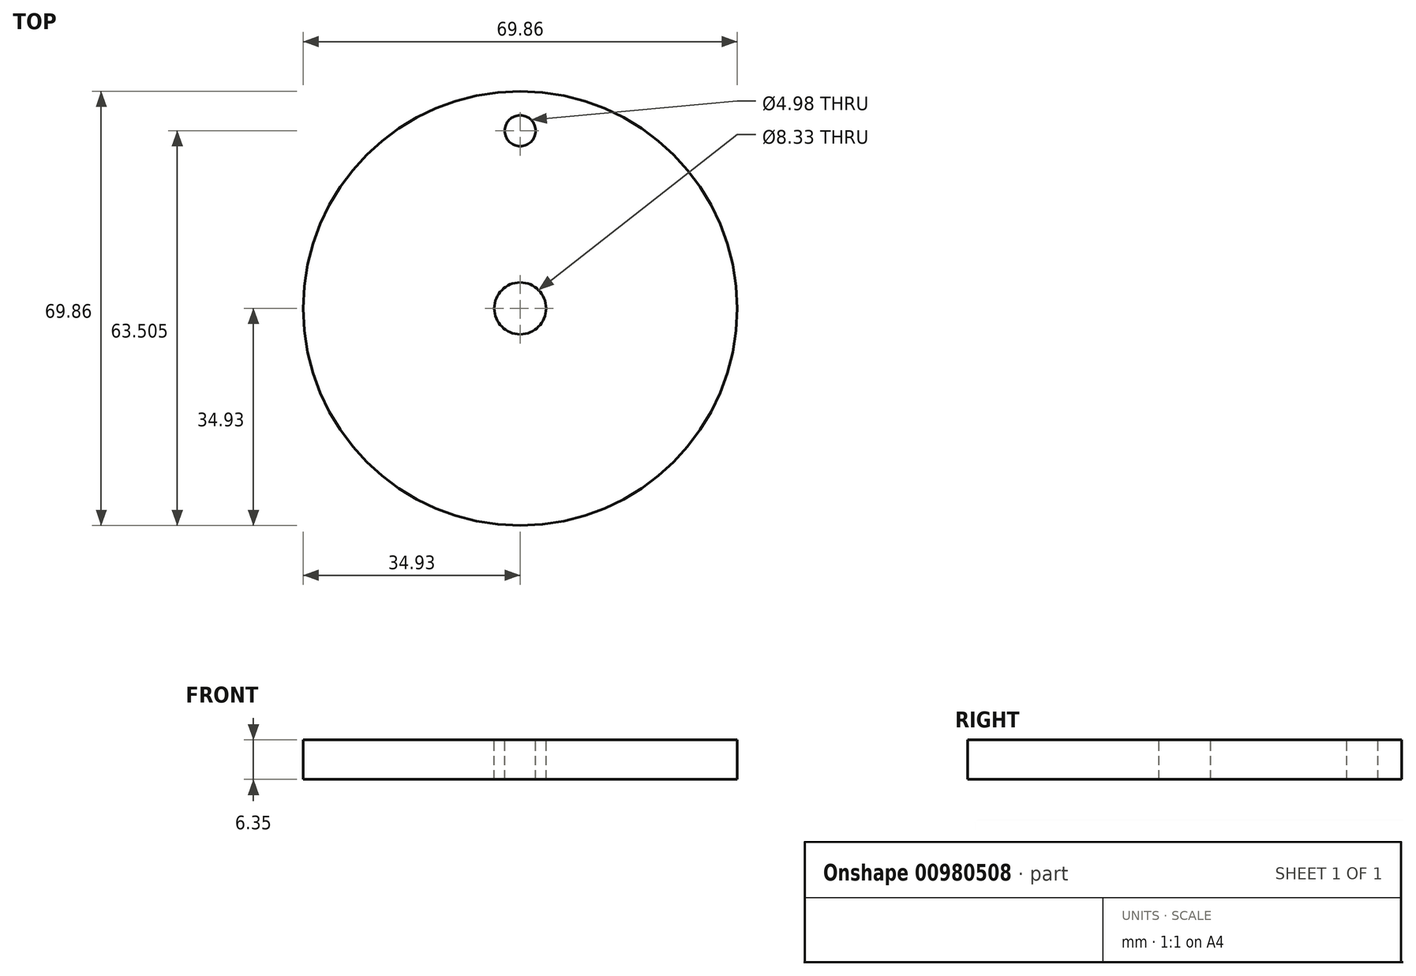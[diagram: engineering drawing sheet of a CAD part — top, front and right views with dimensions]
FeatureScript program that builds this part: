
annotation { "Feature Type Name" : "Feature", "Feature Type Description" : "" }
export const myFeature = defineFeature(function(context is Context, id is Id, definition is map)
    precondition{}
    {
        {
            var Q0;
            Q0=qCreatedBy(makeId("Top.planeOp"),FACE);
            var sketch = newSketch(context, id + "F0", { "sketchPlane" : qUnion([Q0])});
            skCircle(sketch, "E0", {"center": v(0, 0) * mm, "radius": 34.93 * mm});
            skSolve(sketch);
        }
        {
            var Q0;
            Q0=makeQuery(id+"F0.imprint","IMPRINT",FACE,{"disambiguationData":[TD([[makeQuery(id+"F0.imprint","IMPRINT",EDGE,{"derivedFrom":sQuery(id+"F0.wireOp",EDGE,"E0")}),1.0]])]});
            extrude(context, id + "F1", {"entities" : qUnion([Q0]), "depth" : 6.35 * mm, "offsetDistance" : 25.4 * mm});
        }
        {
            var Q0;
            Q0=makeQuery(id+"F1.opExtrude","CAP_FACE",FACE,{"disambiguationData":[OSD([sQuery(id+"F0.wireOp",EDGE,"E0")])],"isStart":false});
            var sketch = newSketch(context, id + "F2", { "sketchPlane" : qUnion([Q0])});
            skPoint(sketch, "E1", {"position": v(0, 28.57) * mm});
            skCircle(sketch, "E2", {"center": v(0, 0) * mm, "radius": 25.4 * mm, "construction": true});
            skLineSegment(sketch, "E3", {"start": v(0, 25.4) * mm, "end": v(0, 31.75) * mm, "construction": true});
            skCircle(sketch, "E4", {"center": v(0, 0) * mm, "radius": 31.75 * mm, "construction": true});
            skSolve(sketch);
        }
        {
            var Q0;
            Q0=sQuery(id+"F2.wireOp",VERTEX,"E1");
            var Q1;
            Q1=makeQuery(id+"F1.opExtrude","SWEPT_BODY",BODY,{"disambiguationData":[OSD([sQuery(id+"F0.wireOp",EDGE,"E0")])]});
            hole(context, id + "F3", {"style" : HoleStyle.SIMPLE, "endStyle" : HoleEndStyle.THROUGH, "standardTappedOrClearance" : lookupTablePath({ "fit" : "Normal (ASME)", "standard" : "ANSI", "size" : "#8", "type" : "Clearance" }), "standardBlindInLast" : lookupTablePath({ "fit" : "Normal", "standard" : "ANSI", "engagement" : "75%", "pitch" : "32 tpi", "size" : "#8", "type" : "Clearance & tapped" }), "holeDiameter" : 4.98 * mm, "majorDiameter" : 6.35 * mm, "isTappedThrough" : true, "tappedDepth" : 16.67 * mm, "tapClearance" : 3, "startFromSketch" : true, "locations" : qUnion([Q0]), "scope" : qUnion([Q1])});
        }
        {
            var Q0;
            Q0=makeQuery(id+"F1.opExtrude","CAP_FACE",FACE,{"disambiguationData":[OSD([sQuery(id+"F0.wireOp",EDGE,"E0")])],"isStart":false});
            var sketch = newSketch(context, id + "F4", { "sketchPlane" : qUnion([Q0])});
            skPoint(sketch, "E5", {"position": v(0, 0) * mm});
            skSolve(sketch);
        }
        {
            var Q0;
            Q0=sQuery(id+"F4.wireOp",VERTEX,"E5");
            var Q1;
            Q1=makeQuery(id+"F1.opExtrude","SWEPT_BODY",BODY,{"disambiguationData":[OSD([sQuery(id+"F0.wireOp",EDGE,"E0")])]});
            hole(context, id + "F5", {"style" : HoleStyle.SIMPLE, "endStyle" : HoleEndStyle.THROUGH, "holeDiameter" : 8.33 * mm, "majorDiameter" : 6.35 * mm, "isTappedThrough" : true, "tappedDepth" : 16.67 * mm, "tapClearance" : 3, "startFromSketch" : true, "locations" : qUnion([Q0]), "scope" : qUnion([Q1])});
        }
    });
